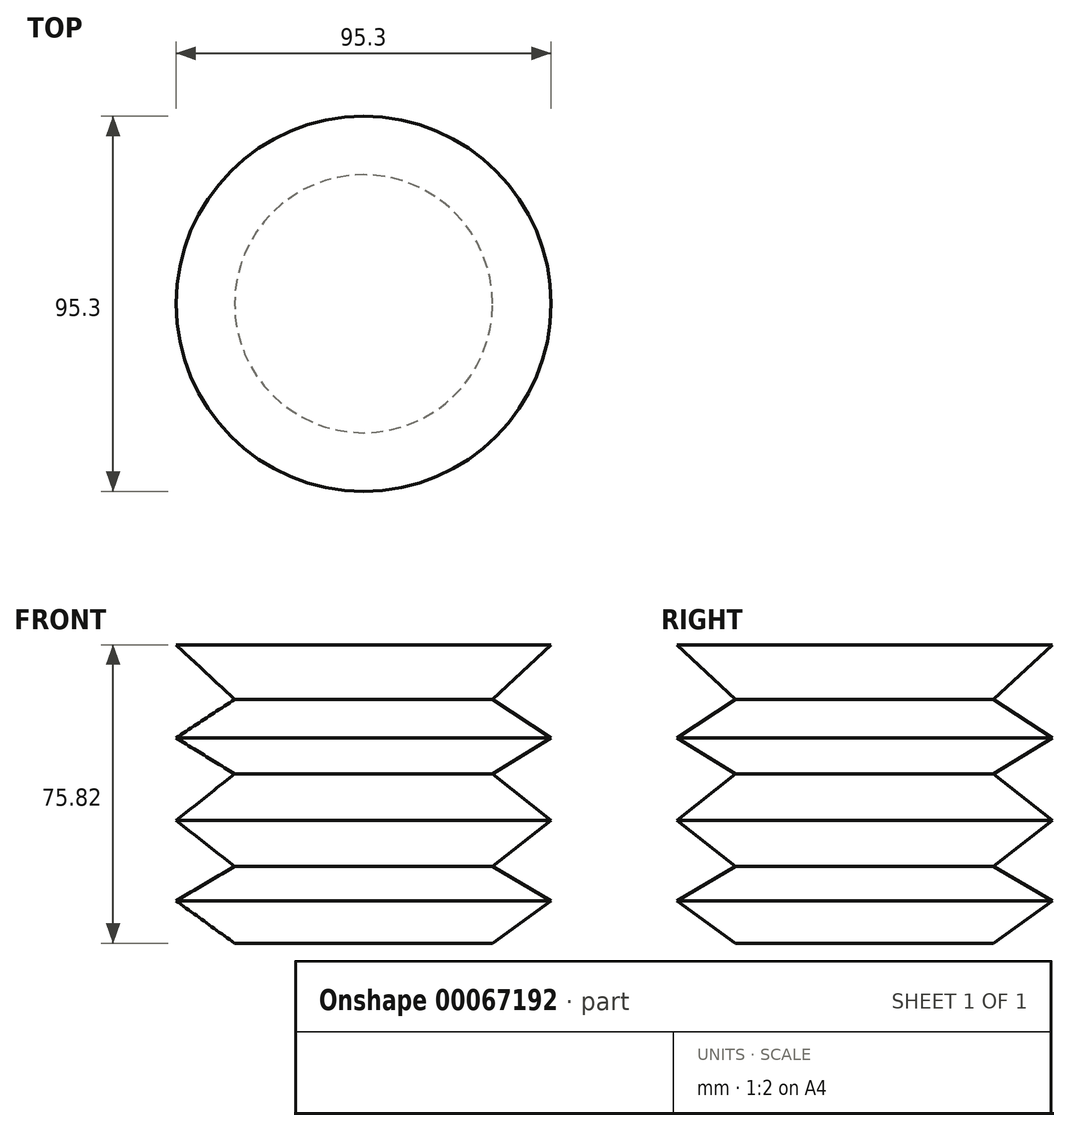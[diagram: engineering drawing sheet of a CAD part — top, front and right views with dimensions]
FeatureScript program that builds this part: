
annotation { "Feature Type Name" : "Feature", "Feature Type Description" : "" }
export const myFeature = defineFeature(function(context is Context, id is Id, definition is map)
    precondition{}
    {
        {
            var Q0;
            Q0=qCreatedBy(makeId("Front.planeOp"),FACE);
            var sketch = newSketch(context, id + "F0", { "sketchPlane" : qUnion([Q0])});
            skLineSegment(sketch, "E0", {"start": v(0, 0) * mm, "end": v(47.65, 0) * mm});
            skLineSegment(sketch, "E1", {"start": v(47.65, 0) * mm, "end": v(32.77, -13.86) * mm});
            skLineSegment(sketch, "E2", {"start": v(32.77, -13.86) * mm, "end": v(47.65, -23.64) * mm});
            skLineSegment(sketch, "E3", {"start": v(47.65, -23.64) * mm, "end": v(32.77, -32.81) * mm});
            skLineSegment(sketch, "E4", {"start": v(32.77, -32.81) * mm, "end": v(47.65, -44.64) * mm});
            skLineSegment(sketch, "E5", {"start": v(47.65, -44.64) * mm, "end": v(32.77, -56.25) * mm});
            skLineSegment(sketch, "E6", {"start": v(32.77, -56.25) * mm, "end": v(47.65, -65.02) * mm});
            skLineSegment(sketch, "E7", {"start": v(47.65, -65.02) * mm, "end": v(32.77, -75.82) * mm});
            skLineSegment(sketch, "E8", {"start": v(32.77, -75.82) * mm, "end": v(0, -75.82) * mm});
            skLineSegment(sketch, "E9", {"start": v(0, -75.82) * mm, "end": v(0, 0) * mm});
            skSolve(sketch);
        }
        {
            var Q0;
            Q0=makeQuery(id+"F0.imprint","IMPRINT",FACE,{"disambiguationData":[TD([[makeQuery(id+"F0.imprint","IMPRINT",EDGE,{"derivedFrom":sQuery(id+"F0.wireOp",EDGE,"E0")}),-1.0]])]});
            var Q1;
            Q1=sQuery(id+"F0.wireOp",EDGE,"E9");
            revolve(context, id + "F1", {"entities" : qUnion([Q0]), "axis" : qUnion([Q1]), "revolveType" : RevolveType.FULL});
        }
    });
